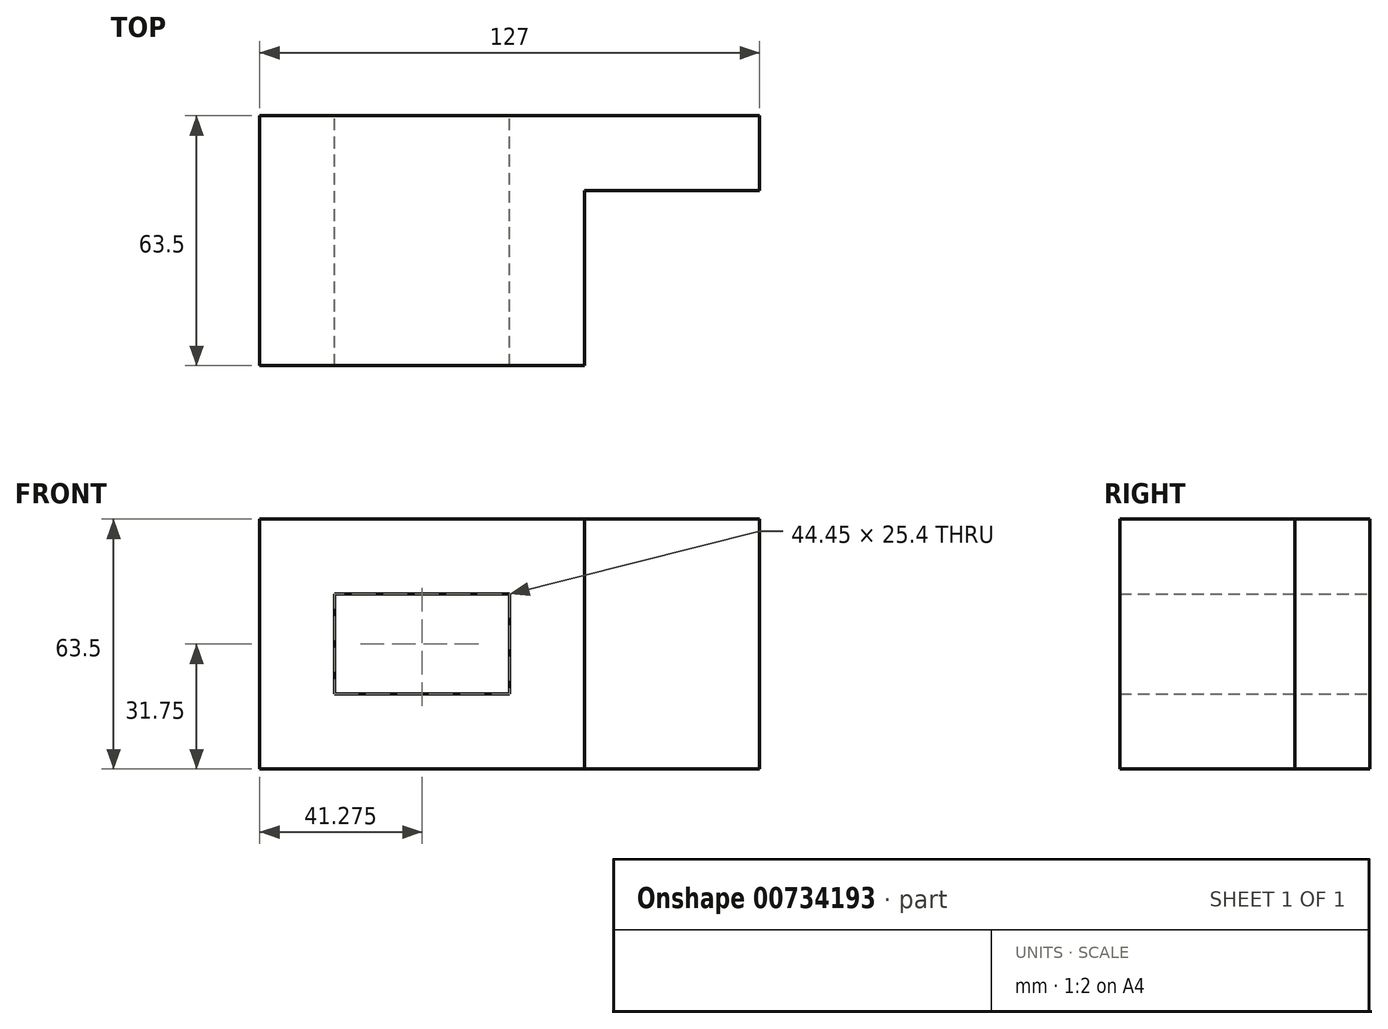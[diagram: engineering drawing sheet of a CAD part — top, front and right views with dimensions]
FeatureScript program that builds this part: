
annotation { "Feature Type Name" : "Feature", "Feature Type Description" : "" }
export const myFeature = defineFeature(function(context is Context, id is Id, definition is map)
    precondition{}
    {
        {
            var Q0;
            Q0=qCreatedBy(makeId("Front.planeOp"),FACE);
            var sketch = newSketch(context, id + "F0", { "sketchPlane" : qUnion([Q0])});
            skLineSegment(sketch, "E0", {"start": v(0, 0) * mm, "end": v(127, 0) * mm});
            skLineSegment(sketch, "E1", {"start": v(127, 0) * mm, "end": v(127, 63.5) * mm});
            skLineSegment(sketch, "E2", {"start": v(127, 63.5) * mm, "end": v(0, 63.5) * mm});
            skLineSegment(sketch, "E3", {"start": v(0, 63.5) * mm, "end": v(0, 0) * mm});
            skLineSegment(sketch, "E4", {"start": v(82.55, 63.5) * mm, "end": v(82.55, 0) * mm});
            skLineSegment(sketch, "E5", {"start": v(19.05, 44.45) * mm, "end": v(19.05, 19.05) * mm});
            skLineSegment(sketch, "E6", {"start": v(63.5, 19.05) * mm, "end": v(19.05, 19.05) * mm});
            skLineSegment(sketch, "E7", {"start": v(63.5, 19.05) * mm, "end": v(63.5, 44.45) * mm});
            skLineSegment(sketch, "E8", {"start": v(63.5, 44.45) * mm, "end": v(19.05, 44.45) * mm});
            skSolve(sketch);
        }
        {
            var Q0;
            {var subQ1=sQuery(id+"F0.wireOp",EDGE,"E3");Q0=makeQuery(id+"F0.imprint","IMPRINT",FACE,{"disambiguationData":[TD([[makeQuery(id+"F0.imprint","IMPRINT",EDGE,{"derivedFrom":subQ1}),1.0]])]});}
            extrude(context, id + "F1", {"entities" : qUnion([Q0]), "depth" : 63.5 * mm, "offsetDistance" : 25.4 * mm});
        }
        {
            var Q0;
            {var subQ0=sQuery(id+"F0.wireOp",EDGE,"E1");Q0=makeQuery(id+"F0.imprint","IMPRINT",FACE,{"disambiguationData":[TD([[makeQuery(id+"F0.imprint","IMPRINT",EDGE,{"derivedFrom":subQ0}),1.0]])]});}
            extrude(context, id + "F2", {"entities" : qUnion([Q0]), "operationType" : NewBodyOperationType.ADD, "depth" : 19.05 * mm, "offsetDistance" : 25.4 * mm});
        }
    });
